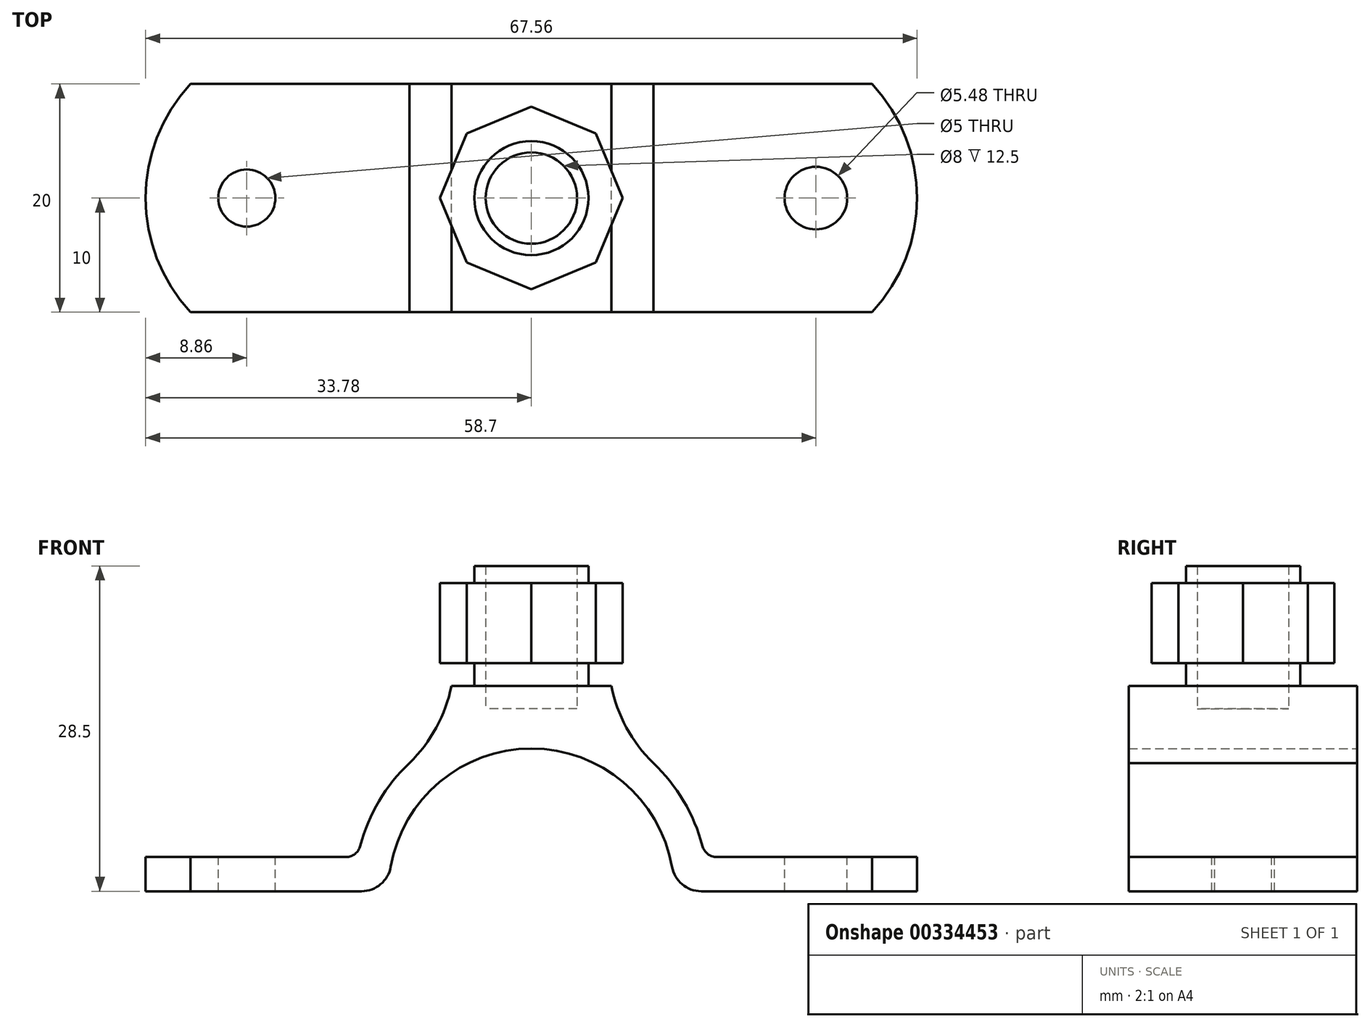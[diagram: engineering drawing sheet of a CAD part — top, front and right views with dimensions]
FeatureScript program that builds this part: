
annotation { "Feature Type Name" : "Feature", "Feature Type Description" : "" }
export const myFeature = defineFeature(function(context is Context, id is Id, definition is map)
    precondition{}
    {
        {
            var Q0;
            Q0=qCreatedBy(makeId("Front.planeOp"),FACE);
            var sketch = newSketch(context, id + "F0", { "sketchPlane" : qUnion([Q0])});
            skArc(sketch, "E0", {"start": v(12.31, 2.15) * mm, "mid": v(0, 12.5) * mm, "end": v(-12.31, 2.15) * mm});
            skArc(sketch, "E1.0", {"start": v(-10.68, 11.24) * mm, "mid": v(-13.34, 7.9) * mm, "end": v(-14.98, 3.97) * mm});
            skLineSegment(sketch, "E2", {"start": v(-14.87, 0) * mm, "end": v(-29.85, 0) * mm});
            skLineSegment(sketch, "E3", {"start": v(-29.85, 0) * mm, "end": v(-29.85, 3) * mm});
            skLineSegment(sketch, "E4", {"start": v(-29.85, 3) * mm, "end": v(-16.24, 3) * mm});
            skLineSegment(sketch, "E5", {"start": v(14.87, 0) * mm, "end": v(29.85, 0) * mm});
            skLineSegment(sketch, "E6", {"start": v(29.85, 0) * mm, "end": v(29.85, 3) * mm});
            skLineSegment(sketch, "E7", {"start": v(29.85, 3) * mm, "end": v(16.24, 3) * mm});
            skLineSegment(sketch, "E8", {"start": v(0, 0) * mm, "end": v(0, 18) * mm, "construction": true});
            skLineSegment(sketch, "E9", {"start": v(-7, 18) * mm, "end": v(7, 18) * mm});
            skArc(sketch, "E10", {"start": v(-10.68, 11.24) * mm, "mid": v(-8.33, 14.34) * mm, "end": v(-7, 18) * mm});
            skArc(sketch, "E11", {"start": v(7, 18) * mm, "mid": v(8.33, 14.34) * mm, "end": v(10.68, 11.24) * mm});
            skArc(sketch, "E12.trimOffspring", {"start": v(14.98, 3.97) * mm, "mid": v(13.34, 7.9) * mm, "end": v(10.68, 11.24) * mm});
            skPoint(sketch, "E13.visualSharp", {"position": v(-15.2, 3) * mm});
            skArc(sketch, "E13.filletArc", {"start": v(-16.24, 3) * mm, "mid": v(-15.45, 3.27) * mm, "end": v(-14.98, 3.97) * mm});
            skPoint(sketch, "E14.visualSharp", {"position": v(15.2, 3) * mm});
            skArc(sketch, "E14.filletArc", {"start": v(14.98, 3.97) * mm, "mid": v(15.45, 3.27) * mm, "end": v(16.24, 3) * mm});
            skPoint(sketch, "E15.visualSharp", {"position": v(-12.5, 0) * mm});
            skArc(sketch, "E15.filletArc", {"start": v(-14.87, 0) * mm, "mid": v(-13.2, 0.6) * mm, "end": v(-12.31, 2.15) * mm});
            skPoint(sketch, "E16.visualSharp", {"position": v(12.5, 0) * mm});
            skArc(sketch, "E16.filletArc", {"start": v(12.31, 2.15) * mm, "mid": v(13.2, 0.6) * mm, "end": v(14.87, 0) * mm});
            skSolve(sketch);
        }
        {
            var Q0;
            Q0=makeQuery(id+"F0.imprint","IMPRINT",FACE,{"disambiguationData":[TD([[makeQuery(id+"F0.imprint","IMPRINT",EDGE,{"derivedFrom":sQuery(id+"F0.wireOp",EDGE,"E0")}),-1.0]])]});
            extrude(context, id + "F1", {"entities" : qUnion([Q0]), "depth" : 20 * mm, "symmetric" : true});
        }
        {
            var Q0;
            Q0=makeQuery(id+"F1.opExtrude","SWEPT_FACE",FACE,{"disambiguationData":[OSD([sQuery(id+"F0.wireOp",EDGE,"E4")])]});
            var sketch = newSketch(context, id + "F2", { "sketchPlane" : qUnion([Q0])});
            skCircle(sketch, "E17", {"center": v(-24.92, 0) * mm, "radius": 2.5 * mm});
            skCircle(sketch, "E18", {"center": v(24.92, 0) * mm, "radius": 2.74 * mm});
            skSolve(sketch);
        }
        {
            var Q0;
            Q0=makeQuery(id+"F2.imprint","IMPRINT",FACE,{"disambiguationData":[TD([[makeQuery(id+"F2.imprint","IMPRINT",EDGE,{"derivedFrom":sQuery(id+"F2.wireOp",EDGE,"E17")}),1.0]])]});
            var Q1;
            Q1=makeQuery(id+"F2.imprint","IMPRINT",FACE,{"disambiguationData":[TD([[makeQuery(id+"F2.imprint","IMPRINT",EDGE,{"derivedFrom":sQuery(id+"F2.wireOp",EDGE,"E18")}),1.0]])]});
            extrude(context, id + "F3", {"entities" : qUnion([Q0, Q1]), "operationType" : NewBodyOperationType.REMOVE, "oppositeDirection" : true, "depth" : 25 * mm});
        }
        {
            var Q0;
            Q0=makeQuery(id+"F1.opExtrude","SWEPT_FACE",FACE,{"disambiguationData":[OSD([sQuery(id+"F0.wireOp",EDGE,"E4")])]});
            var sketch = newSketch(context, id + "F4", { "sketchPlane" : qUnion([Q0])});
            skArc(sketch, "E19", {"start": v(-29.85, 10) * mm, "mid": v(-33.78, 0) * mm, "end": v(-29.85, -10) * mm});
            skArc(sketch, "E20", {"start": v(30, -9.99) * mm, "mid": v(33.93, -0.05) * mm, "end": v(30.1, 9.92) * mm});
            skSolve(sketch);
        }
        {
            var Q0;
            Q0=makeQuery(id+"F4.imprint","IMPRINT",FACE,{"disambiguationData":[TD([[makeQuery(id+"F4.imprint","IMPRINT",EDGE,{"derivedFrom":sQuery(id+"F4.wireOp",EDGE,"E19")}),1.0]])]});
            extrude(context, id + "F5", {"entities" : qUnion([Q0]), "operationType" : NewBodyOperationType.ADD, "oppositeDirection" : true, "depth" : 3 * mm});
        }
        {
            var Q0;
            Q0=makeQuery(id+"F1.opExtrude","SWEPT_FACE",FACE,{"disambiguationData":[OSD([sQuery(id+"F0.wireOp",EDGE,"E7")])]});
            var sketch = newSketch(context, id + "F6", { "sketchPlane" : qUnion([Q0])});
            skArc(sketch, "E21", {"start": v(29.85, -10) * mm, "mid": v(33.78, 0) * mm, "end": v(29.85, 10) * mm});
            skSolve(sketch);
        }
        {
            var Q0;
            Q0=makeQuery(id+"F6.imprint","IMPRINT",FACE,{"disambiguationData":[TD([[makeQuery(id+"F6.imprint","IMPRINT",EDGE,{"derivedFrom":sQuery(id+"F6.wireOp",EDGE,"E21")}),1.0]])]});
            extrude(context, id + "F7", {"entities" : qUnion([Q0]), "operationType" : NewBodyOperationType.ADD, "oppositeDirection" : true, "depth" : 3 * mm});
        }
        {
            var Q0;
            Q0=makeQuery(id+"F1.opExtrude","SWEPT_FACE",FACE,{"disambiguationData":[OSD([sQuery(id+"F0.wireOp",EDGE,"E9")])]});
            var sketch = newSketch(context, id + "F8", { "sketchPlane" : qUnion([Q0])});
            skCircle(sketch, "E22", {"center": v(0, 0) * mm, "radius": 5 * mm});
            skSolve(sketch);
        }
        {
            var Q0;
            Q0=makeQuery(id+"F8.imprint","IMPRINT",FACE,{"disambiguationData":[TD([[makeQuery(id+"F8.imprint","IMPRINT",EDGE,{"derivedFrom":sQuery(id+"F8.wireOp",EDGE,"E22")}),1.0]])]});
            extrude(context, id + "F9", {"entities" : qUnion([Q0]), "operationType" : NewBodyOperationType.ADD, "depth" : 2 * mm});
        }
        {
            var Q0;
            Q0=makeQuery(id+"F9.opExtrude","CAP_FACE",FACE,{"disambiguationData":[OSD([sQuery(id+"F8.wireOp",EDGE,"E22")])],"isStart":false});
            var sketch = newSketch(context, id + "F10", { "sketchPlane" : qUnion([Q0])});
            skCircle(sketch, "E23.cCircle", {"center": v(0, 0) * mm, "radius": 8 * mm, "construction": true});
            skLineSegment(sketch, "E23.0", {"start": v(0, 8) * mm, "end": v(5.66, 5.66) * mm});
            skLineSegment(sketch, "E23.1", {"start": v(5.66, 5.66) * mm, "end": v(8, 0) * mm});
            skLineSegment(sketch, "E23.2", {"start": v(8, 0) * mm, "end": v(5.66, -5.66) * mm});
            skLineSegment(sketch, "E23.3", {"start": v(5.66, -5.66) * mm, "end": v(0, -8) * mm});
            skLineSegment(sketch, "E23.4", {"start": v(0, -8) * mm, "end": v(-5.66, -5.66) * mm});
            skLineSegment(sketch, "E23.5", {"start": v(-5.66, -5.66) * mm, "end": v(-8, 0) * mm});
            skLineSegment(sketch, "E23.6", {"start": v(-8, 0) * mm, "end": v(-5.66, 5.66) * mm});
            skLineSegment(sketch, "E23.7", {"start": v(-5.66, 5.66) * mm, "end": v(0, 8) * mm});
            skSolve(sketch);
        }
        {
            var Q0;
            Q0 = qSketchRegion(id + "F10", true);
            extrude(context, id + "F11", {"entities" : qUnion([Q0]), "operationType" : NewBodyOperationType.ADD, "depth" : 7 * mm});
        }
        {
            var Q0;
            Q0=makeQuery(id+"F11.opExtrude","CAP_FACE",FACE,{"disambiguationData":[OSD([sQuery(id+"F10.wireOp",EDGE,"E23.0"),sQuery(id+"F10.wireOp",EDGE,"E23.1"),sQuery(id+"F10.wireOp",EDGE,"E23.2"),sQuery(id+"F10.wireOp",EDGE,"E23.3"),sQuery(id+"F10.wireOp",EDGE,"E23.4"),sQuery(id+"F10.wireOp",EDGE,"E23.5"),sQuery(id+"F10.wireOp",EDGE,"E23.6"),sQuery(id+"F10.wireOp",EDGE,"E23.7")])],"isStart":false});
            var sketch = newSketch(context, id + "F12", { "sketchPlane" : qUnion([Q0])});
            skCircle(sketch, "E24", {"center": v(0, 0) * mm, "radius": 4 * mm});
            skCircle(sketch, "E25.0", {"center": v(0, 0) * mm, "radius": 5 * mm});
            skSolve(sketch);
        }
        {
            var Q0;
            Q0=makeQuery(id+"F12.imprint","IMPRINT",FACE,{"disambiguationData":[TD([[makeQuery(id+"F12.imprint","IMPRINT",EDGE,{"derivedFrom":sQuery(id+"F12.wireOp",EDGE,"E24")}),-1.0]])]});
            extrude(context, id + "F13", {"entities" : qUnion([Q0]), "operationType" : NewBodyOperationType.ADD, "depth" : 1.5 * mm});
        }
        {
            var Q0;
            Q0=makeQuery(id+"F13.boolean.opBoolean","SPLIT",FACE,{"disambiguationData":[TD([makeQuery(id+"F13.opExtrude","SWEPT_FACE",FACE,{"disambiguationData":[OSD([sQuery(id+"F12.wireOp",EDGE,"E24")])]})])],"derivedFrom":makeQuery(id+"F11.opExtrude","CAP_FACE",FACE,{"disambiguationData":[OSD([sQuery(id+"F10.wireOp",EDGE,"E23.0"),sQuery(id+"F10.wireOp",EDGE,"E23.1"),sQuery(id+"F10.wireOp",EDGE,"E23.2"),sQuery(id+"F10.wireOp",EDGE,"E23.3"),sQuery(id+"F10.wireOp",EDGE,"E23.4"),sQuery(id+"F10.wireOp",EDGE,"E23.5"),sQuery(id+"F10.wireOp",EDGE,"E23.6"),sQuery(id+"F10.wireOp",EDGE,"E23.7")])],"isStart":false})});
            extrude(context, id + "F14", {"entities" : qUnion([Q0]), "operationType" : NewBodyOperationType.REMOVE, "oppositeDirection" : true, "depth" : 11 * mm});
        }
    });
